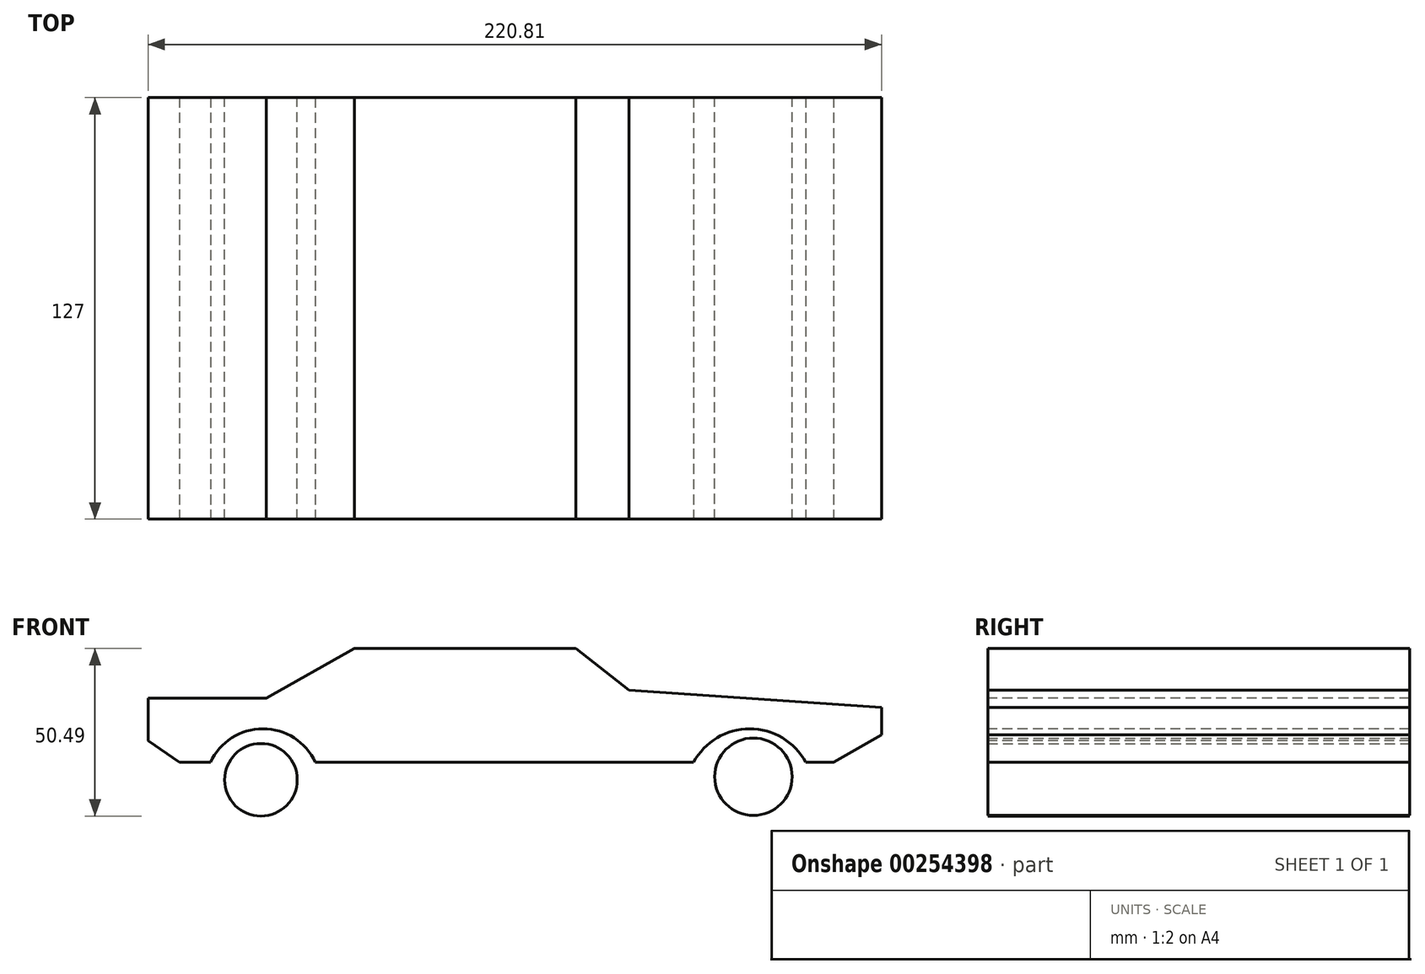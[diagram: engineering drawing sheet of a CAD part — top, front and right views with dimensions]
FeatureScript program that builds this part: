
annotation { "Feature Type Name" : "Feature", "Feature Type Description" : "" }
export const myFeature = defineFeature(function(context is Context, id is Id, definition is map)
    precondition{}
    {
        {
            var Q0;
            Q0=qCreatedBy(makeId("Front.planeOp"),FACE);
            var sketch = newSketch(context, id + "F0", { "sketchPlane" : qUnion([Q0])});
            skLineSegment(sketch, "E0", {"start": v(-215.44, 20.9) * mm, "end": v(38.56, 20.9) * mm});
            skLineSegment(sketch, "E1", {"start": v(38.56, 20.9) * mm, "end": v(38.56, -42.6) * mm});
            skLineSegment(sketch, "E2", {"start": v(38.56, -42.6) * mm, "end": v(-215.44, -42.6) * mm});
            skLineSegment(sketch, "E3", {"start": v(-215.44, -42.6) * mm, "end": v(-215.44, 20.9) * mm});
            skSolve(sketch);
        }
        {
            var Q0;
            Q0=makeQuery(id+"F0.imprint","IMPRINT",FACE,{"disambiguationData":[TD([[makeQuery(id+"F0.imprint","IMPRINT",EDGE,{"derivedFrom":sQuery(id+"F0.wireOp",EDGE,"E0")}),-1.0]])]});
            extrude(context, id + "F1", {"entities" : qUnion([Q0]), "depth" : 127 * mm});
        }
        {
            var Q0;
            Q0=makeQuery(id+"F1.opExtrude","CAP_FACE",FACE,{"disambiguationData":[OSD([sQuery(id+"F0.wireOp",EDGE,"E0"),sQuery(id+"F0.wireOp",EDGE,"E1"),sQuery(id+"F0.wireOp",EDGE,"E2"),sQuery(id+"F0.wireOp",EDGE,"E3")])],"isStart":false});
            var sketch = newSketch(context, id + "F2", { "sketchPlane" : qUnion([Q0])});
            skLineSegment(sketch, "E4", {"start": v(38.56, -10.86) * mm, "end": v(-37.47, -5.69) * mm});
            skLineSegment(sketch, "E5", {"start": v(-37.47, -5.69) * mm, "end": v(-53.42, 6.9) * mm});
            skLineSegment(sketch, "E6", {"start": v(-53.42, 6.9) * mm, "end": v(-120.13, 6.9) * mm});
            skLineSegment(sketch, "E7", {"start": v(-120.13, 6.9) * mm, "end": v(-146.7, -8.05) * mm});
            skLineSegment(sketch, "E8", {"start": v(-146.7, -8.05) * mm, "end": v(-182.25, -8.05) * mm});
            skLineSegment(sketch, "E9", {"start": v(-182.25, -8.05) * mm, "end": v(-182.25, -27.4) * mm});
            skLineSegment(sketch, "E10", {"start": v(-182.25, -27.4) * mm, "end": v(38.56, -27.4) * mm});
            skLineSegment(sketch, "E11", {"start": v(38.56, -27.4) * mm, "end": v(38.56, -10.86) * mm});
            skSolve(sketch);
        }
        {
            var Q0;
            {var subQ2=sQuery(id+"F2.wireOp",EDGE,"E4");Q0=makeQuery(id+"F2.imprint","IMPRINT",FACE,{"disambiguationData":[TD([[makeQuery(id+"F2.imprint","IMPRINT",EDGE,{"derivedFrom":subQ2}),-1.0]])]});}
            extrude(context, id + "F3", {"entities" : qUnion([Q0]), "operationType" : NewBodyOperationType.REMOVE, "oppositeDirection" : true, "depth" : 127 * mm});
        }
        {
            var Q0;
            Q0=makeQuery(id+"F1.opExtrude","CAP_FACE",FACE,{"disambiguationData":[OSD([sQuery(id+"F0.wireOp",EDGE,"E0"),sQuery(id+"F0.wireOp",EDGE,"E1"),sQuery(id+"F0.wireOp",EDGE,"E2"),sQuery(id+"F0.wireOp",EDGE,"E3")])],"isStart":false});
            var sketch = newSketch(context, id + "F4", { "sketchPlane" : qUnion([Q0])});
            skArc(sketch, "E12", {"start": v(-131.9, -27.4) * mm, "mid": v(-147.68, -17.3) * mm, "end": v(-163.46, -27.4) * mm});
            skArc(sketch, "E13", {"start": v(15.75, -27.4) * mm, "mid": v(-1.12, -17.3) * mm, "end": v(-18, -27.4) * mm});
            skSolve(sketch);
        }
        {
            var Q0;
            {var subQ0=sQuery(id+"F4.wireOp",EDGE,"E12");Q0=makeQuery(id+"F4.imprint","IMPRINT",FACE,{"disambiguationData":[TD([[makeQuery(id+"F4.imprint","IMPRINT",EDGE,{"derivedFrom":subQ0}),1.0]])]});}
            var Q1;
            {var subQ0=sQuery(id+"F4.wireOp",EDGE,"E13");Q1=makeQuery(id+"F4.imprint","IMPRINT",FACE,{"disambiguationData":[TD([[makeQuery(id+"F4.imprint","IMPRINT",EDGE,{"derivedFrom":subQ0}),1.0]])]});}
            extrude(context, id + "F5", {"entities" : qUnion([Q0, Q1]), "operationType" : NewBodyOperationType.REMOVE, "oppositeDirection" : true, "depth" : 127 * mm});
        }
        {
            var Q0;
            Q0=makeQuery(id+"F1.opExtrude","CAP_FACE",FACE,{"disambiguationData":[OSD([sQuery(id+"F0.wireOp",EDGE,"E0"),sQuery(id+"F0.wireOp",EDGE,"E1"),sQuery(id+"F0.wireOp",EDGE,"E2"),sQuery(id+"F0.wireOp",EDGE,"E3")])],"isStart":false});
            var sketch = newSketch(context, id + "F6", { "sketchPlane" : qUnion([Q0])});
            skLineSegment(sketch, "E14", {"start": v(-172.86, -27.4) * mm, "end": v(-182.25, -20.9) * mm});
            skLineSegment(sketch, "E15", {"start": v(38.56, -19.12) * mm, "end": v(24.1, -27.4) * mm});
            skSolve(sketch);
        }
        {
            var Q0;
            {var subQ0=sQuery(id+"F6.wireOp",EDGE,"E14");Q0=makeQuery(id+"F6.imprint","IMPRINT",FACE,{"disambiguationData":[TD([[makeQuery(id+"F6.imprint","IMPRINT",EDGE,{"derivedFrom":subQ0}),1.0]])]});}
            var Q1;
            {var subQ0=sQuery(id+"F6.wireOp",EDGE,"E15");Q1=makeQuery(id+"F6.imprint","IMPRINT",FACE,{"disambiguationData":[TD([[makeQuery(id+"F6.imprint","IMPRINT",EDGE,{"derivedFrom":subQ0}),1.0]])]});}
            extrude(context, id + "F7", {"entities" : qUnion([Q0, Q1]), "operationType" : NewBodyOperationType.REMOVE, "oppositeDirection" : true, "depth" : 127 * mm});
        }
        {
            var Q0;
            Q0=qCreatedBy(makeId("Front.planeOp"),FACE);
            var sketch = newSketch(context, id + "F8", { "sketchPlane" : qUnion([Q0])});
            skCircle(sketch, "E16", {"center": v(-148.3, -32.65) * mm, "radius": 10.94 * mm});
            skCircle(sketch, "E17", {"center": v(0, -31.73) * mm, "radius": 11.67 * mm});
            skSolve(sketch);
        }
        {
            var Q0;
            Q0=makeQuery(id+"F8.imprint","IMPRINT",FACE,{"disambiguationData":[TD([[makeQuery(id+"F8.imprint","IMPRINT",EDGE,{"derivedFrom":sQuery(id+"F8.wireOp",EDGE,"E16")}),1.0]])]});
            var Q1;
            Q1=makeQuery(id+"F8.imprint","IMPRINT",FACE,{"disambiguationData":[TD([[makeQuery(id+"F8.imprint","IMPRINT",EDGE,{"derivedFrom":sQuery(id+"F8.wireOp",EDGE,"E17")}),1.0]])]});
            extrude(context, id + "F9", {"entities" : qUnion([Q0, Q1]), "depth" : 127 * mm});
        }
    });
